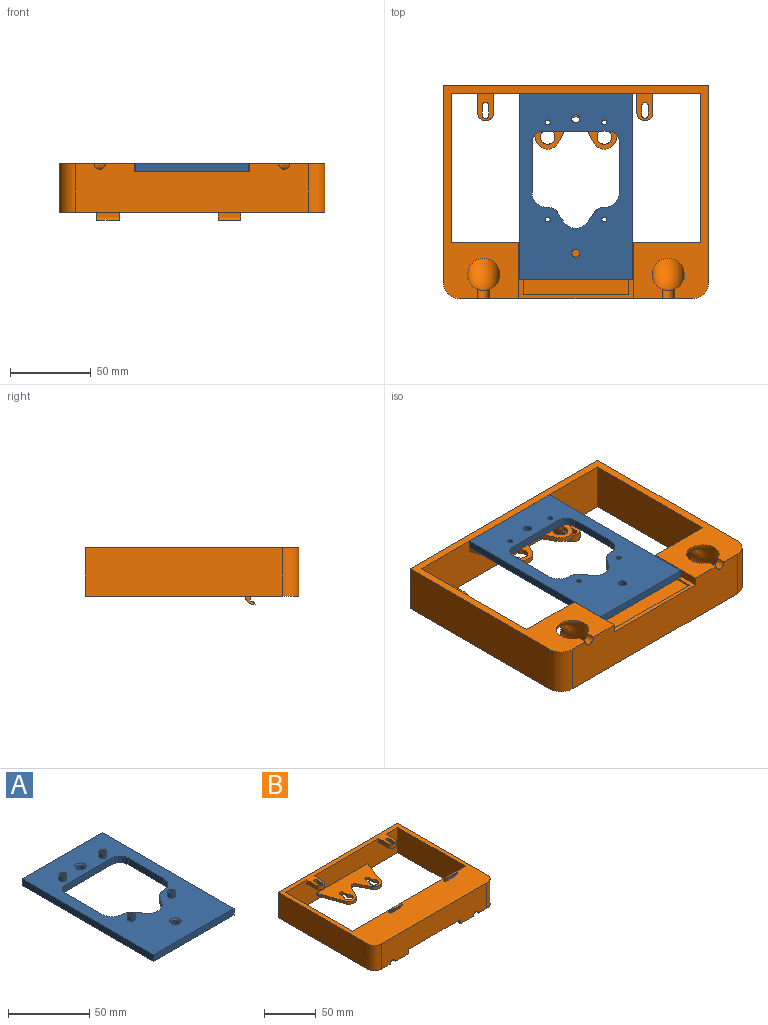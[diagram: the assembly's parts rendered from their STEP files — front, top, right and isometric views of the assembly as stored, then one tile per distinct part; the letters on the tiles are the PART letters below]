
ASSEMBLY  parts=2 mates=1
PART A: 36 faces, bbox 70x115x8.5 mm
  f0: plane 115x70mm, normal (0,0,-1), area 5256.7mm2, adj f1,f2,f3,f4,f6,f9,f12,f15
  f1: plane 70x5mm, normal (0,1,0), area 350mm2, adj f0,f2,f4,f5
  f2: plane 115x5mm, normal (-1,0,0), area 575mm2, adj f0,f1,f3,f5
  f3: plane 70x5mm, normal (0,-1,0), area 350mm2, adj f0,f2,f4,f5
  f4: plane 115x5mm, normal (1,0,0), area 575mm2, adj f0,f1,f3,f5
  f5: plane 115x70mm, normal (0,0,1), area 5176.4mm2, adj f1,f2,f3,f4,f7,f10,f13,f16
  f6: cylinder r=1.5mm len=8.5mm, axis (0,0,-1), area 80.1mm2, adj f0,f8
  f7: cylinder r=2.38mm len=4.75mm, axis (0,0,-1), area 52.2mm2, adj f5,f8
  f8: plane 4.75x4.75mm, normal (0,0,1), area 10.7mm2, adj f6,f7
  f9: cylinder r=1.5mm len=8.5mm, axis (0,0,-1), area 80.1mm2, adj f0,f11
  f10: cylinder r=2.38mm len=4.75mm, axis (0,0,-1), area 52.2mm2, adj f5,f11
  f11: plane 4.75x4.75mm, normal (0,0,1), area 10.7mm2, adj f9,f10
  f12: cylinder r=1.5mm len=8.5mm, axis (0,0,-1), area 80.1mm2, adj f0,f14
  f13: cylinder r=2.38mm len=4.75mm, axis (0,0,-1), area 52.2mm2, adj f5,f14
  f14: plane 4.75x4.75mm, normal (0,0,1), area 10.7mm2, adj f12,f13
  f15: cylinder r=1.5mm len=8.5mm, axis (0,0,-1), area 80.1mm2, adj f0,f17
  f16: cylinder r=2.38mm len=4.75mm, axis (0,0,-1), area 52.2mm2, adj f5,f17
  f17: plane 4.75x4.75mm, normal (0,0,1), area 10.7mm2, adj f15,f16
  f18: cylinder r=2.5mm len=5mm, axis (0,0,-1), area 62.8mm2, adj f0,f21
  f19: cylinder r=2.5mm len=5mm, axis (0,0,-1), area 62.8mm2, adj f0,f20
  f20: cone r=2.5mm half-angle=45deg, axis (0,0,1), area 26.7mm2, adj f5,f19
  f21: cone r=2.5mm half-angle=45deg, axis (0,0,1), area 26.7mm2, adj f5,f18
  f22: plane 40x5mm, normal (0,-1,0), area 200mm2, adj f0,f5,f23,f35
  f23: cylinder r=7mm len=7mm, axis (0,0,-1), area 55mm2, adj f0,f5,f22,f24
  f24: plane 31.1x5mm, normal (-1,0,0), area 155.5mm2, adj f0,f5,f23,f25
  f25: cylinder r=9mm len=9mm, axis (0,0,-1), area 70.7mm2, adj f0,f5,f24,f26
  f26: plane 5x0.27mm, normal (0,1,0), area 1.4mm2, adj f0,f5,f25,f27
  f27: cylinder r=7.5mm len=6.12mm, axis (0,0,-1), area 35.8mm2, adj f0,f5,f26,f28
  f28: plane 6.02x5mm, normal (-0.82,0.58,0), area 36.9mm2, adj f0,f5,f27,f29
  f29: cylinder r=9mm len=14.68mm, axis (0,0,-1), area 85.8mm2, adj f0,f5,f28,f30
  f30: plane 6.02x5mm, normal (0.82,0.58,0), area 36.9mm2, adj f0,f5,f29,f31
  f31: cylinder r=7.5mm len=6.12mm, axis (0,0,-1), area 35.8mm2, adj f0,f5,f30,f32
  f32: plane 5x0.27mm, normal (0,1,0), area 1.4mm2, adj f0,f5,f31,f33
  f33: cylinder r=9mm len=9mm, axis (0,0,-1), area 70.7mm2, adj f0,f5,f32,f34
  f34: plane 31.1x5mm, normal (1,0,0), area 155.5mm2, adj f0,f5,f33,f35
  f35: cylinder r=7mm len=7mm, axis (0,0,-1), area 55mm2, adj f0,f5,f22,f34
PART B: 95 faces, bbox 164.2x132x35 mm
  f0: plane 164.2x132mm, normal (0,0,-1), area 4258.8mm2, adj f1,f2,f19,f20,f21,f22,f23,f24
  f1: plane 154.2x30mm, normal (0,1,0), area 3432.7mm2, adj f0,f16,f17,f18,f20,f26,f61,f67
  f2: plane 144.2x30mm, normal (0,-1,0), area 3932.5mm2, adj f0,f16,f18,f24,f25,f87,f88,f93
  f3: plane 6x5mm, normal (-1,0,0), area 14.1mm2, adj f18,f43,f81,f82,f84,f85
  f4: plane 6x5mm, normal (1,0,0), area 14.1mm2, adj f18,f43,f81,f82,f84,f85
  f5: plane 6x5mm, normal (1,0,0), area 14.1mm2, adj f18,f45,f79,f80,f83,f86
  f6: plane 5.26x2mm, normal (-1,0,0), area 10.5mm2, adj f7,f9,f17,f78
  f7: cylinder r=4.5mm len=9mm, axis (0,0,-1), area 45.9mm2, adj f6,f8,f17,f78
  f8: plane 5.26x2mm, normal (1,0,0), area 10.5mm2, adj f7,f9,f17,f78
  f9: cylinder r=2.5mm len=5mm, axis (0,0,-1), area 15.7mm2, adj f6,f8,f17,f78
  f10: cylinder r=2.5mm len=5mm, axis (0,0,-1), area 15.7mm2, adj f11,f13,f17,f78
  f11: plane 5.26x2mm, normal (-1,0,0), area 10.5mm2, adj f10,f12,f17,f78
  f12: cylinder r=4.5mm len=9mm, axis (0,0,-1), area 45.9mm2, adj f11,f13,f17,f78
  f13: plane 5.26x2mm, normal (1,0,0), area 10.5mm2, adj f10,f12,f17,f78
  f14: plane 70x34.5mm, normal (0,0,-1), area 1477.5mm2, adj f19,f46,f47,f48,f49,f50,f51,f52
  f15: plane 70x34.5mm, normal (0,0,1), area 1477.5mm2, adj f19,f46,f47,f48,f49,f50,f51,f52
  f16: plane 71x56.5mm, normal (0,0,-1), area 652.9mm2, adj f1,f2,f61,f62,f63,f64,f65,f66
  f17: plane 70x21.5mm, normal (0,0,1), area 687.4mm2, adj f1,f6,f7,f8,f9,f10,f11,f12
  f18: plane 164.2x132mm, normal (0,0,1), area 7606.5mm2, adj f1,f2,f3,f4,f5,f19,f20,f21
  f19: plane 154.2x30mm, normal (0,-1,0), area 4316mm2, adj f0,f14,f15,f18,f20,f26,f27,f33
  f20: plane 92x30mm, normal (-1,0,0), area 2760mm2, adj f0,f1,f18,f19
  f21: plane 122x30mm, normal (1,0,0), area 3660mm2, adj f0,f18,f22,f25
  f22: plane 164.2x30mm, normal (0,1,0), area 4926mm2, adj f0,f18,f21,f23
  f23: plane 122x30mm, normal (-1,0,0), area 3660mm2, adj f0,f18,f22,f24
  f24: cylinder r=10mm len=30mm, axis (0,0,1), area 471.2mm2, adj f0,f2,f18,f23
  f25: cylinder r=10mm len=30mm, axis (0,0,1), area 471.2mm2, adj f0,f2,f18,f21
  f26: plane 92x30mm, normal (1,0,0), area 2760mm2, adj f0,f1,f18,f19
  f27: plane 12x5mm, normal (-1,0,0), area 60mm2, adj f18,f19,f28,f34
  f28: cylinder r=5mm len=10mm, axis (0,0,1), area 78.5mm2, adj f18,f27,f33,f34
  f29: cylinder r=2mm len=5mm, axis (0,0,1), area 31.4mm2, adj f18,f30,f32,f34
  f30: plane 6x5mm, normal (-1,0,0), area 30mm2, adj f18,f29,f31,f34
  f31: cylinder r=2mm len=5mm, axis (0,0,1), area 31.4mm2, adj f18,f30,f32,f34
  f32: plane 6x5mm, normal (1,0,0), area 30mm2, adj f18,f29,f31,f34
  f33: plane 12x5mm, normal (1,0,0), area 60mm2, adj f18,f19,f28,f34
  f34: plane 17x10mm, normal (0,0,-1), area 122.7mm2, adj f19,f27,f28,f29,f30,f31,f32,f33
  f35: plane 12x5mm, normal (-1,0,0), area 60mm2, adj f18,f19,f36,f42
  f36: cylinder r=5mm len=10mm, axis (0,0,1), area 78.5mm2, adj f18,f35,f41,f42
  f37: cylinder r=2mm len=5mm, axis (0,0,1), area 31.4mm2, adj f18,f38,f40,f42
  f38: plane 6x5mm, normal (-1,0,0), area 30mm2, adj f18,f37,f39,f42
  f39: cylinder r=2mm len=5mm, axis (0,0,1), area 31.4mm2, adj f18,f38,f40,f42
  f40: plane 6x5mm, normal (1,0,0), area 30mm2, adj f18,f37,f39,f42
  f41: plane 12x5mm, normal (1,0,0), area 60mm2, adj f18,f19,f36,f42
  f42: plane 17x10mm, normal (0,0,-1), area 122.7mm2, adj f19,f35,f36,f37,f38,f39,f40,f41
  f43: plane 14x1mm, normal (0,0,1), area 14mm2, adj f3,f4,f84,f85
  f44: plane 6x5mm, normal (-1,0,0), area 14.1mm2, adj f18,f45,f79,f80,f83,f86
  f45: plane 14x1mm, normal (0,0,1), area 14mm2, adj f5,f44,f83,f86
  f46: plane 5.26x3mm, normal (1,0,0), area 15.8mm2, adj f14,f15,f47,f49
  f47: cylinder r=2.5mm len=5mm, axis (0,0,-1), area 23.6mm2, adj f14,f15,f46,f48
  f48: plane 5.26x3mm, normal (-1,0,0), area 15.8mm2, adj f14,f15,f47,f49
  f49: cylinder r=4.5mm len=9mm, axis (0,0,-1), area 68.9mm2, adj f14,f15,f46,f48
  f50: cylinder r=2.5mm len=5mm, axis (0,0,-1), area 23.6mm2, adj f14,f15,f51,f53
  f51: plane 5.26x3mm, normal (-1,0,0), area 15.8mm2, adj f14,f15,f50,f52
  f52: cylinder r=4.5mm len=9mm, axis (0,0,-1), area 68.9mm2, adj f14,f15,f51,f53
  f53: plane 5.26x3mm, normal (1,0,0), area 15.8mm2, adj f14,f15,f50,f52
  f54: cylinder r=7.5mm len=13.7mm, axis (0,0,-1), area 52.1mm2, adj f14,f15,f55,f60
  f55: plane 13.85x7.34mm, normal (-0.88,-0.47,0), area 47mm2, adj f14,f15,f54,f56
  f56: cylinder r=4mm len=7.07mm, axis (0,0,-1), area 26mm2, adj f14,f15,f55,f57
  f57: plane 13.85x7.34mm, normal (0.88,-0.47,0), area 47mm2, adj f14,f15,f56,f58
  f58: cylinder r=7.5mm len=13.7mm, axis (0,0,-1), area 52.1mm2, adj f14,f15,f57,f59
  f59: plane 29.5x10.43mm, normal (-0.94,-0.33,0), area 93.9mm2, adj f14,f15,f19,f58
  f60: plane 29.5x10.43mm, normal (0.94,-0.33,0), area 93.9mm2, adj f14,f15,f19,f54
  f61: plane 17.95x11.13mm, normal (0.85,0.53,0), area 63.4mm2, adj f1,f16,f17,f62
  f62: cylinder r=7.5mm len=13.13mm, axis (0,0,-1), area 48.1mm2, adj f16,f17,f61,f63
  f63: plane 14.8x7.14mm, normal (-0.9,0.43,0), area 49.3mm2, adj f16,f17,f62,f64
  f64: cylinder r=4mm len=7.2mm, axis (0,0,-1), area 26.9mm2, adj f16,f17,f63,f65
  f65: plane 14.8x7.14mm, normal (0.9,0.43,0), area 49.3mm2, adj f16,f17,f64,f66
  f66: cylinder r=7.5mm len=13.13mm, axis (0,0,-1), area 48.1mm2, adj f16,f17,f65,f67
  f67: plane 17.95x11.13mm, normal (-0.85,0.53,0), area 63.4mm2, adj f1,f16,f17,f66
  f68: plane 17.35x10.75mm, normal (-0.85,-0.53,0), area 20.4mm2, adj f16,f69,f77,f78
  f69: plane 31.79x1mm, normal (-1,0,0), area 31.8mm2, adj f16,f68,f70,f78
  f70: plane 65x1mm, normal (0,1,0), area 65mm2, adj f16,f69,f71,f78
  f71: plane 31.79x1mm, normal (1,0,0), area 31.8mm2, adj f16,f70,f72,f78
  f72: plane 17.35x10.75mm, normal (0.85,-0.53,0), area 20.4mm2, adj f16,f71,f73,f78
  f73: cylinder r=5mm len=8.75mm, axis (0,0,-1), area 10.7mm2, adj f16,f72,f74,f78
  f74: plane 14.8x7.14mm, normal (-0.9,-0.43,0), area 16.4mm2, adj f16,f73,f75,f78
  f75: cylinder r=6.5mm len=11.71mm, axis (0,0,-1), area 14.6mm2, adj f16,f74,f76,f78
  f76: plane 14.8x7.14mm, normal (0.9,-0.43,0), area 16.4mm2, adj f16,f75,f77,f78
  f77: cylinder r=5mm len=8.75mm, axis (0,0,-1), area 10.7mm2, adj f16,f68,f76,f78
  f78: plane 65x51.5mm, normal (0,0,-1), area 2519.5mm2, adj f6,f7,f8,f9,f10,f11,f12,f13
  f79: plane 14x0.17mm, normal (0,0,-1), area 2.4mm2, adj f5,f44,f80,f83
  f80: plane 14x3mm, normal (0,-1,0), area 42mm2, adj f5,f18,f44,f79
  f81: plane 14x3mm, normal (0,-1,0), area 42mm2, adj f3,f4,f18,f82
  f82: plane 14x0.17mm, normal (0,0,-1), area 2.4mm2, adj f3,f4,f81,f84
  f83: cylinder r=3mm len=14mm, axis (1,0,0), area 51.7mm2, adj f5,f44,f45,f79
  f84: cylinder r=3mm len=14mm, axis (1,0,0), area 51.7mm2, adj f3,f4,f43,f82
  f85: cylinder r=5mm len=14mm, axis (1,0,0), area 110mm2, adj f3,f4,f18,f43
  f86: cylinder r=5mm len=14mm, axis (1,0,0), area 110mm2, adj f5,f18,f44,f45
  f87: cylinder r=3.5mm len=7mm, axis (0,-1,0), area 59.8mm2, adj f0,f2,f91
  f88: cylinder r=3.5mm len=7mm, axis (0,-1,0), area 59.8mm2, adj f0,f2,f89
  f89: torus R=15mm, axis (1,0,0), area 1460.9mm2, adj f0,f88,f90
  f90: cylinder r=10mm len=20mm, axis (0,-1,0), area 314.2mm2, adj f1,f89
  f91: torus R=15mm, axis (1,0,0), area 1460.9mm2, adj f0,f87,f92
  f92: cylinder r=10mm len=20mm, axis (0,-1,0), area 314.2mm2, adj f1,f91
  f93: plane 35x5mm, normal (-1,0,0), area 175mm2, adj f0,f1,f2,f16
  f94: plane 35x5mm, normal (1,0,0), area 175mm2, adj f0,f1,f2,f16
PLACE A rot(axis=(0,1,0),180deg) t=(167.92,52.69,2.53)mm
PLACE B rot(axis=(0,1,0),180deg) t=(161.47,13.02,-27.47)mm
MATE revolute A.f6 <-> B.f50  axis (0,0,-1) through (185.62,92.02,-2.47)mm
